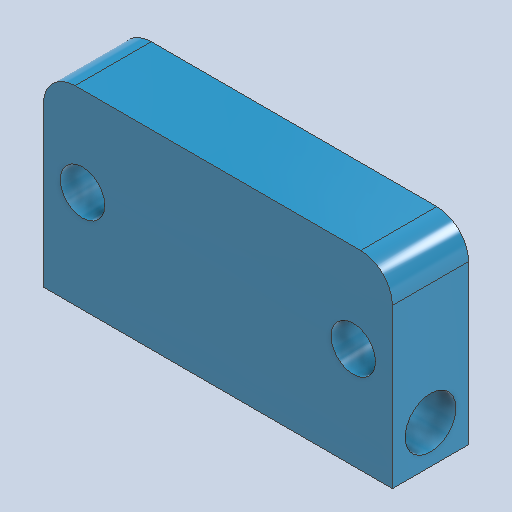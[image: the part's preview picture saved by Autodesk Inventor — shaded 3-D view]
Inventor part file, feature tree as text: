
AUTODESK INVENTOR PART (.ipt)
format: ipt  version: 2022 (Build 260153000, 153)  size: 156,672 bytes
history: native  units: mm
features: extrude x3, sketch x3, other x1, fillet x1
ambient origin geometry x8: Origin, YZ Plane, XZ Plane, XY Plane, X Axis, Y Axis, Z Axis, Center Point
bodies: Body1 (feature_tree)
feature tree (8):
  other  "Sólido1"
  extrude  "Extrusión1"  Depth=55.0mm
  fillet  "Empalme1"  Radius=20.0mm
  extrude  "Extrusión5"  Depth=5.0mm
  extrude  "Extrusión6"  Depth=10.0mm TaperAngle=0.0deg
  sketch  "Boceto1"  dims[d0=7.0mm d1=55.0mm d3=20.0mm]
  sketch  "Boceto7"  dims[d4=12.0mm d5=0.0mm d15=5.0mm]
  sketch  "Boceto8"  dims[d23=42.67mm d24=10.0mm d25=0.0mm d26=8.0mm d27=6.0mm d29=55.0mm d30=0.0mm d32=6.0mm]
